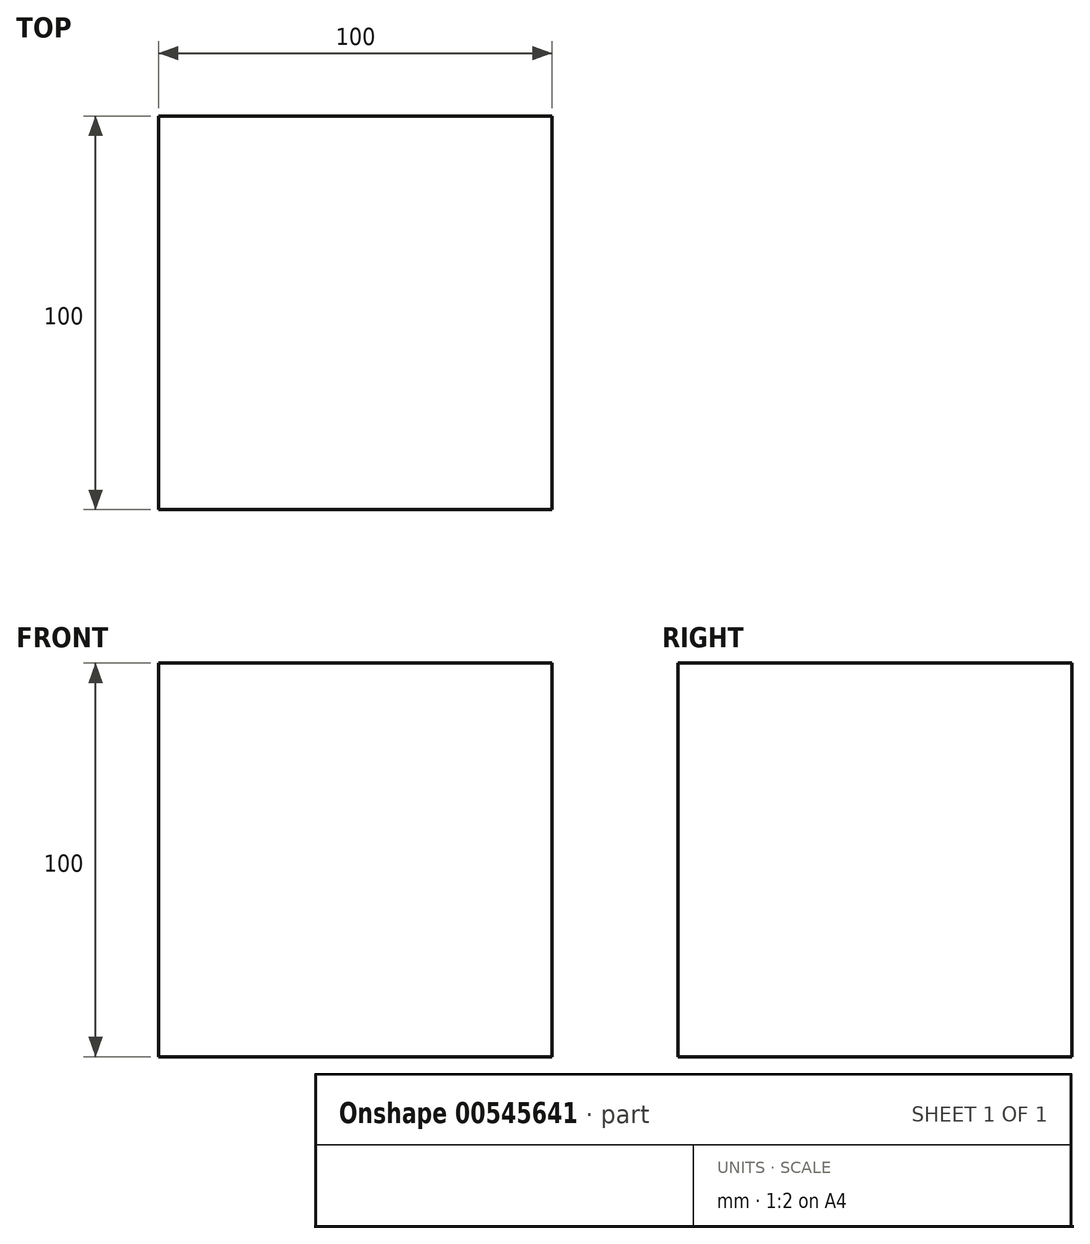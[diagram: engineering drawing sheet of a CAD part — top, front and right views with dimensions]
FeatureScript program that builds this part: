
annotation { "Feature Type Name" : "Feature", "Feature Type Description" : "" }
export const myFeature = defineFeature(function(context is Context, id is Id, definition is map)
    precondition{}
    {
        {
            var Q0;
            Q0=qCreatedBy(makeId("Front.planeOp"),FACE);
            var sketch = newSketch(context, id + "F0", { "sketchPlane" : qUnion([Q0])});
            skLineSegment(sketch, "E0.bottom", {"start": v(-50, 50) * mm, "end": v(50, 50) * mm});
            skLineSegment(sketch, "E0.top", {"start": v(-50, -50) * mm, "end": v(50, -50) * mm});
            skLineSegment(sketch, "E0.left", {"start": v(-50, 50) * mm, "end": v(-50, -50) * mm});
            skLineSegment(sketch, "E0.right", {"start": v(50, 50) * mm, "end": v(50, -50) * mm});
            skLineSegment(sketch, "E1.bottom", {"start": v(50, 50) * mm, "end": v(50, 50) * mm});
            skLineSegment(sketch, "E1.top", {"start": v(50, 45.84) * mm, "end": v(50, 45.84) * mm});
            skLineSegment(sketch, "E1.left", {"start": v(50, 50) * mm, "end": v(50, 45.84) * mm});
            skLineSegment(sketch, "E1.right", {"start": v(50, 50) * mm, "end": v(50, 45.84) * mm});
            skSolve(sketch);
        }
        {
            var Q0;
            Q0 = qSketchRegion(id + "F0", true);
            extrude(context, id + "F1", {"entities" : qUnion([Q0]), "oppositeDirection" : true, "depth" : 100 * mm, "offsetDistance" : 25 * mm});
        }
    });
